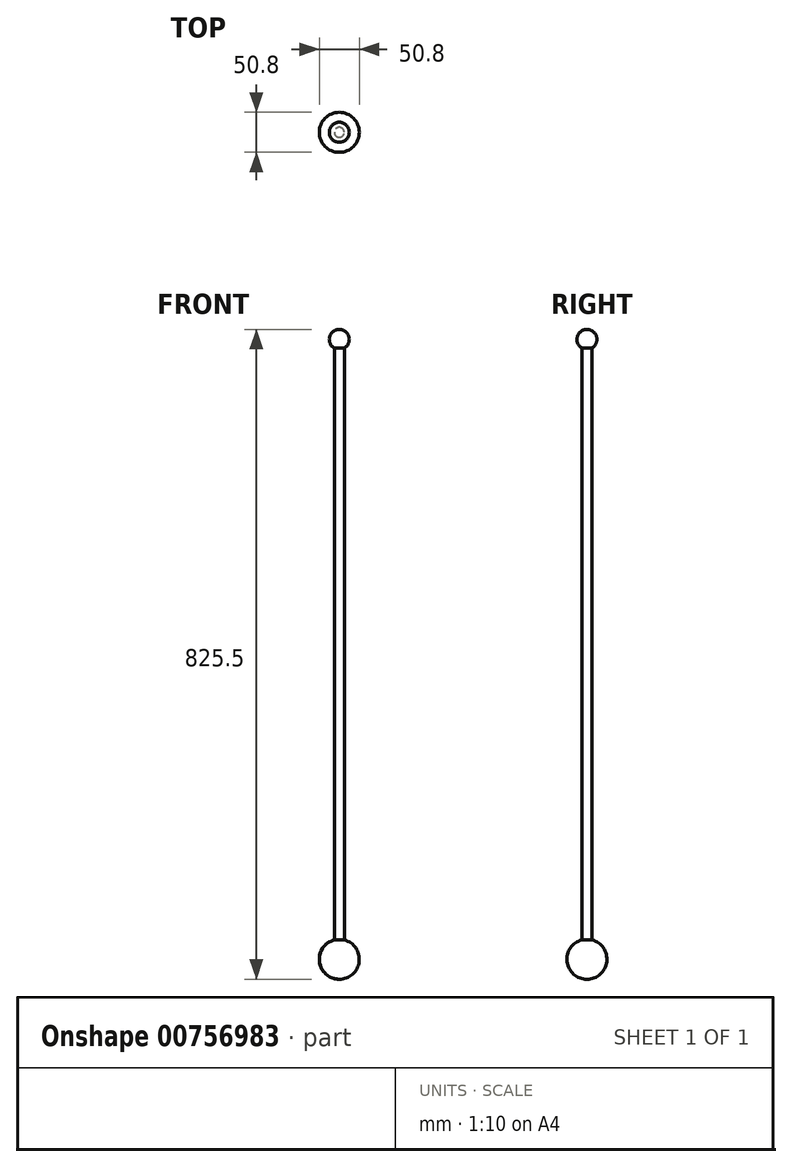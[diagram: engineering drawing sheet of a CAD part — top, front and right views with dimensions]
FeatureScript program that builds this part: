
annotation { "Feature Type Name" : "Feature", "Feature Type Description" : "" }
export const myFeature = defineFeature(function(context is Context, id is Id, definition is map)
    precondition{}
    {
        {
            var Q0;
            Q0=qCreatedBy(makeId("Front.planeOp"),FACE);
            var sketch = newSketch(context, id + "F0", { "sketchPlane" : qUnion([Q0])});
            skLineSegment(sketch, "E0.bottom", {"start": v(0, 0) * mm, "end": v(12.7, 0) * mm});
            skLineSegment(sketch, "E0.top", {"start": v(0, 787.4) * mm, "end": v(12.7, 787.4) * mm});
            skLineSegment(sketch, "E0.left", {"start": v(0, 0) * mm, "end": v(0, 787.4) * mm});
            skLineSegment(sketch, "E0.right", {"start": v(12.7, 0) * mm, "end": v(12.7, 787.4) * mm});
            skCircle(sketch, "E1", {"center": v(6.35, 787.4) * mm, "radius": 12.7 * mm});
            skCircle(sketch, "E2", {"center": v(6.35, 0) * mm, "radius": 25.4 * mm});
            skLineSegment(sketch, "E3", {"start": v(6.35, -25.4) * mm, "end": v(6.35, 800.1) * mm});
            skSolve(sketch);
        }
        {
            var Q0;
            {var subQ0=sQuery(id+"F0.wireOp",EDGE,"E0.right");var subQ1=sQuery(id+"F0.wireOp",EDGE,"E0.top");var subQ2=makeQuery(id+"F0.imprint","INTERSECT",VERTEX,{"derivedFrom":[subQ1,subQ0]});Q0=makeQuery(id+"F0.imprint","IMPRINT",FACE,{"disambiguationData":[TD([[makeQuery(id+"F0.imprint","IMPRINT",EDGE,{"disambiguationData":[TD([[subQ2,1.0]])],"derivedFrom":subQ1}),1.0]])]});}
            var Q1;
            {var subQ0=sQuery(id+"F0.wireOp",EDGE,"E0.right");var subQ1=sQuery(id+"F0.wireOp",EDGE,"E0.top");var subQ2=makeQuery(id+"F0.imprint","INTERSECT",VERTEX,{"derivedFrom":[subQ1,subQ0]});Q1=makeQuery(id+"F0.imprint","IMPRINT",FACE,{"disambiguationData":[TD([[makeQuery(id+"F0.imprint","IMPRINT",EDGE,{"disambiguationData":[TD([[subQ2,1.0]])],"derivedFrom":subQ1}),-1.0]])]});}
            var Q2;
            {var subQ0=sQuery(id+"F0.wireOp",EDGE,"E2");var subQ1=sQuery(id+"F0.wireOp",EDGE,"E0.right");var subQ2=makeQuery(id+"F0.imprint","INTERSECT",VERTEX,{"derivedFrom":[subQ1,subQ0]});Q2=makeQuery(id+"F0.imprint","IMPRINT",FACE,{"disambiguationData":[TD([[makeQuery(id+"F0.imprint","IMPRINT",EDGE,{"disambiguationData":[TD([[subQ2,-1.0]])],"derivedFrom":subQ1}),1.0]])]});}
            var Q3;
            {var subQ0=sQuery(id+"F0.wireOp",EDGE,"E0.right");var subQ1=sQuery(id+"F0.wireOp",EDGE,"E0.bottom");var subQ2=makeQuery(id+"F0.imprint","INTERSECT",VERTEX,{"derivedFrom":[subQ1,subQ0]});Q3=makeQuery(id+"F0.imprint","IMPRINT",FACE,{"disambiguationData":[TD([[makeQuery(id+"F0.imprint","IMPRINT",EDGE,{"disambiguationData":[TD([[subQ2,1.0]])],"derivedFrom":subQ1}),1.0]])]});}
            var Q4;
            {var subQ0=sQuery(id+"F0.wireOp",EDGE,"E0.right");var subQ1=sQuery(id+"F0.wireOp",EDGE,"E0.bottom");var subQ2=makeQuery(id+"F0.imprint","INTERSECT",VERTEX,{"derivedFrom":[subQ1,subQ0]});Q4=makeQuery(id+"F0.imprint","IMPRINT",FACE,{"disambiguationData":[TD([[makeQuery(id+"F0.imprint","IMPRINT",EDGE,{"disambiguationData":[TD([[subQ2,1.0]])],"derivedFrom":subQ1}),-1.0]])]});}
            var Q5;
            Q5=sQuery(id+"F0.wireOp",EDGE,"E3");
            revolve(context, id + "F1", {"surfaceOperationType" : NewSurfaceOperationType.NEW, "entities" : qUnion([Q0, Q1, Q2, Q3, Q4]), "axis" : qUnion([Q5]), "revolveType" : RevolveType.FULL});
        }
    });
